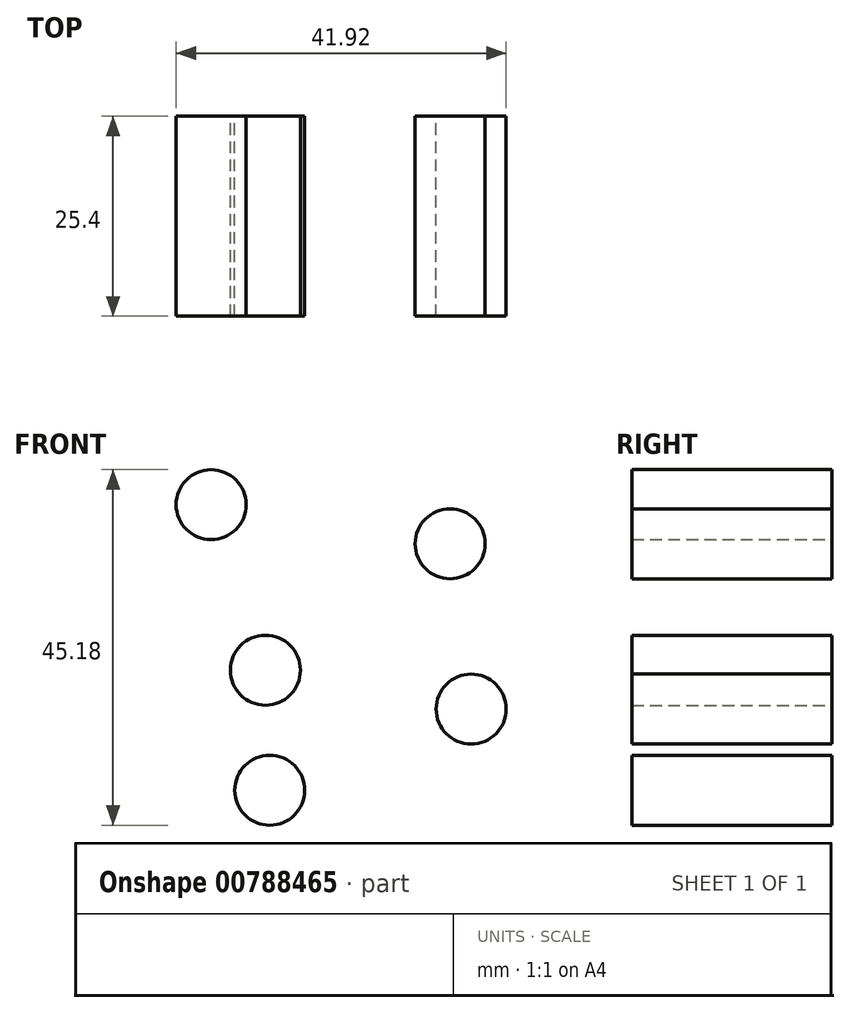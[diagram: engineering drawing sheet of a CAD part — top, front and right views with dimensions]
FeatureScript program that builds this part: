
annotation { "Feature Type Name" : "Feature", "Feature Type Description" : "" }
export const myFeature = defineFeature(function(context is Context, id is Id, definition is map)
    precondition{}
    {
        {
            var Q0;
            Q0=qCreatedBy(makeId("Front.planeOp"),FACE);
            var sketch = newSketch(context, id + "F0", { "sketchPlane" : qUnion([Q0])});
            skCircle(sketch, "E0", {"center": v(-34.06, 26.04) * mm, "radius": 4.45 * mm});
            skCircle(sketch, "E1", {"center": v(-33.51, 10.79) * mm, "radius": 4.45 * mm});
            skCircle(sketch, "E2", {"center": v(-10.6, 42.1) * mm, "radius": 4.45 * mm});
            skCircle(sketch, "E3", {"center": v(-40.96, 47.07) * mm, "radius": 4.45 * mm});
            skCircle(sketch, "E4", {"center": v(-7.92, 21.1) * mm, "radius": 4.45 * mm});
            skSolve(sketch);
        }
        {
            var Q0;
            Q0 = qSketchRegion(id + "F0", true);
            extrude(context, id + "F1", {"entities" : qUnion([Q0]), "depth" : 25.4 * mm, "offsetDistance" : 25.4 * mm});
        }
    });
